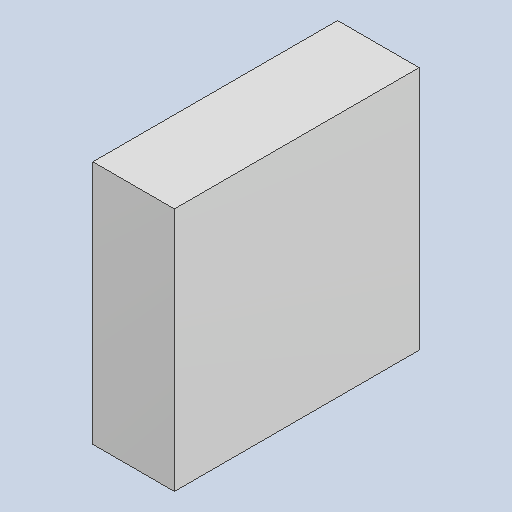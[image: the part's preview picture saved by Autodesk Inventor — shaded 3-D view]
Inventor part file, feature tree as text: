
AUTODESK INVENTOR PART (.ipt)
format: ipt  version: 2023.4 (Build 274418000, 418)  size: 81,408 bytes
history: native  units: mm
features: extrude x1
ambient origin geometry x8: Origin, YZ Plane, XZ Plane, XY Plane, X Axis, Y Axis, Z Axis, Center Point
bodies: Solid1 (feature_tree)
feature tree (1):
  extrude  "Extruded_21"  [1 undecoded]
note: 1 required parameter value undecoded (feature->parameter linkage not recoverable at this tier; creation-order binding heuristic only, values carry confidence <= 0.55)
